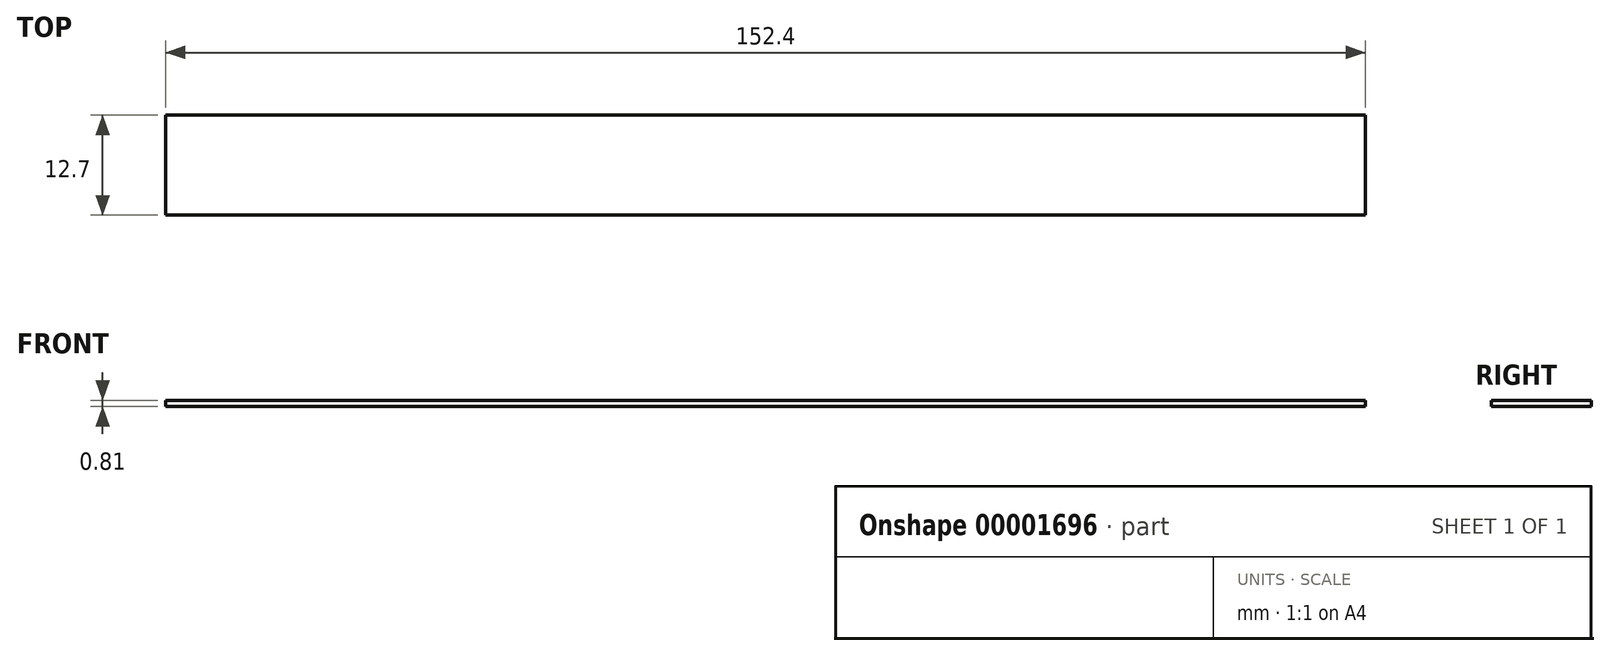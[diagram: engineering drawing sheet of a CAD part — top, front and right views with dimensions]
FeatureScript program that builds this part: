
annotation { "Feature Type Name" : "Feature", "Feature Type Description" : "" }
export const myFeature = defineFeature(function(context is Context, id is Id, definition is map)
    precondition{}
    {
        {
            var Q0;
            Q0=qCreatedBy(makeId("Top.planeOp"),FACE);
            var sketch = newSketch(context, id + "F0", { "sketchPlane" : qUnion([Q0])});
            skLineSegment(sketch, "E0.bottom", {"start": v(-76.2, 6.35) * mm, "end": v(76.2, 6.35) * mm});
            skLineSegment(sketch, "E0.top", {"start": v(-76.2, -6.35) * mm, "end": v(76.2, -6.35) * mm});
            skLineSegment(sketch, "E0.left", {"start": v(-76.2, 6.35) * mm, "end": v(-76.2, -6.35) * mm});
            skLineSegment(sketch, "E0.right", {"start": v(76.2, 6.35) * mm, "end": v(76.2, -6.35) * mm});
            skLineSegment(sketch, "E1", {"start": v(76.2, 6.35) * mm, "end": v(-76.2, -6.35) * mm, "construction": true});
            skSolve(sketch);
        }
        {
            var Q0;
            Q0 = qSketchRegion(id + "F0", true);
            extrude(context, id + "F1", {"entities" : qUnion([Q0]), "depth" : 0.81 * mm});
        }
    });
